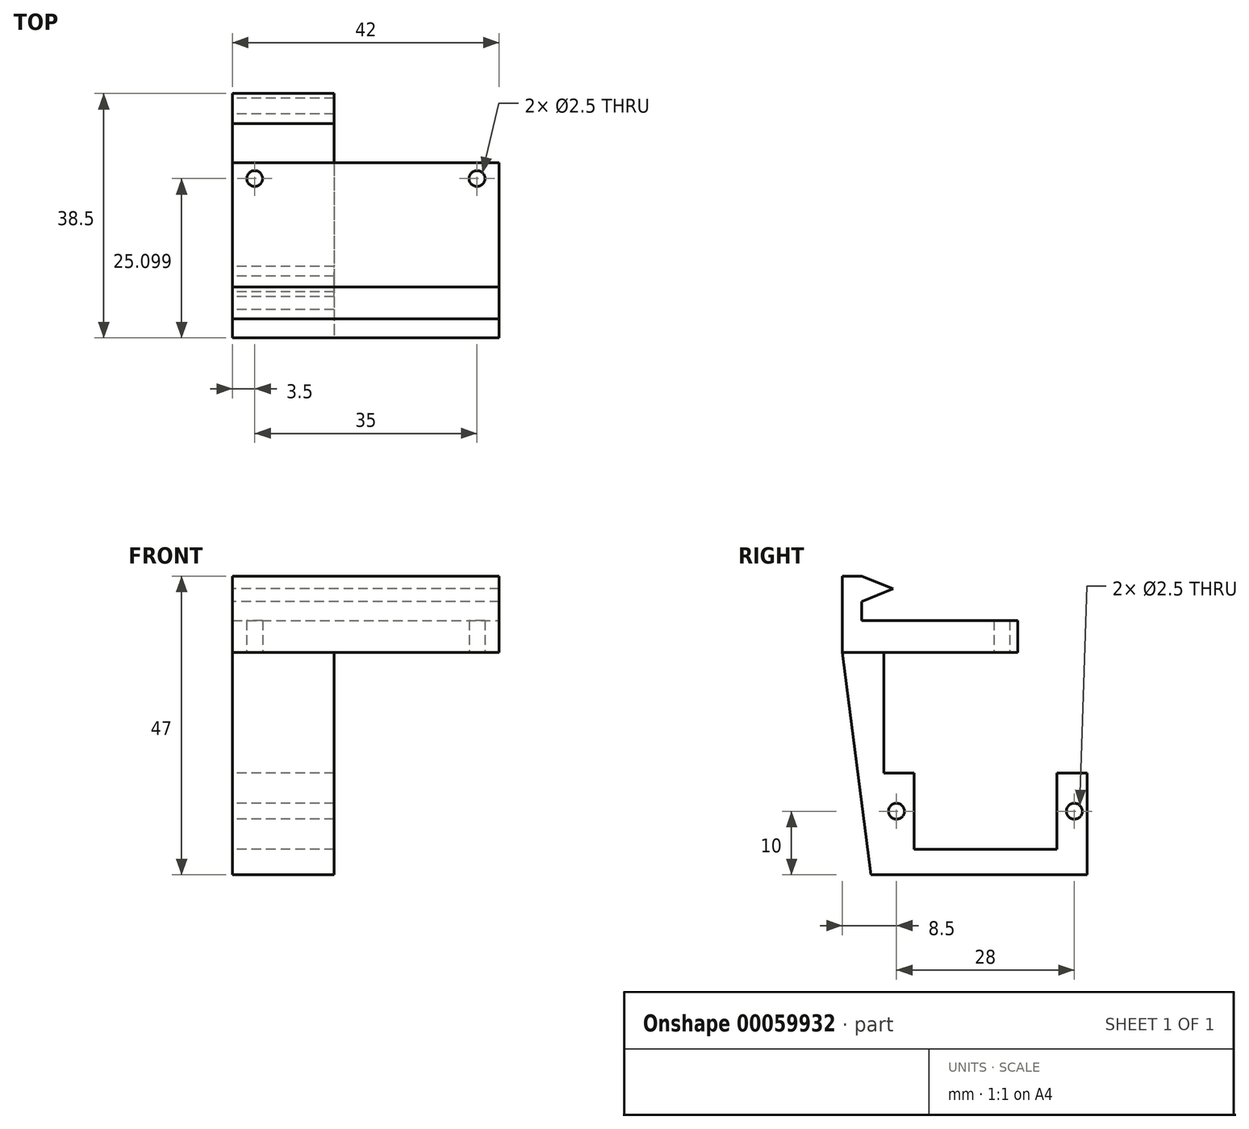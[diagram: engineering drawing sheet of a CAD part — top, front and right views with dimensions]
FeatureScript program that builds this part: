
annotation { "Feature Type Name" : "Feature", "Feature Type Description" : "" }
export const myFeature = defineFeature(function(context is Context, id is Id, definition is map)
    precondition{}
    {
        {
            var Q0;
            Q0=qCreatedBy(makeId("Top.planeOp"),FACE);
            var sketch = newSketch(context, id + "F0", { "sketchPlane" : qUnion([Q0])});
            skLineSegment(sketch, "E0.bottom", {"start": v(0, 0) * mm, "end": v(42, 0) * mm});
            skLineSegment(sketch, "E0.top", {"start": v(0, 24.6) * mm, "end": v(42, 24.6) * mm});
            skLineSegment(sketch, "E0.left", {"start": v(0, 0) * mm, "end": v(0, 24.6) * mm});
            skLineSegment(sketch, "E0.right", {"start": v(42, 0) * mm, "end": v(42, 24.6) * mm});
            skCircle(sketch, "E1", {"center": v(3.5, 22.1) * mm, "radius": 1.25 * mm});
            skCircle(sketch, "E2", {"center": v(38.5, 22.1) * mm, "radius": 1.25 * mm});
            skLineSegment(sketch, "E3", {"start": v(0, 22.1) * mm, "end": v(3.5, 22.1) * mm, "construction": true});
            skLineSegment(sketch, "E4", {"start": v(3.5, 22.1) * mm, "end": v(38.5, 22.1) * mm, "construction": true});
            skLineSegment(sketch, "E5", {"start": v(38.5, 22.1) * mm, "end": v(42, 22.1) * mm, "construction": true});
            skSolve(sketch);
        }
        {
            var Q0;
            Q0=makeQuery(id+"F0.imprint","IMPRINT",FACE,{"disambiguationData":[TD([[makeQuery(id+"F0.imprint","IMPRINT",EDGE,{"derivedFrom":sQuery(id+"F0.wireOp",EDGE,"E0.bottom")}),1.0]])]});
            extrude(context, id + "F1", {"entities" : qUnion([Q0]), "depth" : 5 * mm});
        }
        {
            var Q0;
            Q0=makeQuery(id+"F1.opExtrude","SWEPT_FACE",FACE,{"disambiguationData":[OSD([sQuery(id+"F0.wireOp",EDGE,"E0.left")])]});
            var sketch = newSketch(context, id + "F2", { "sketchPlane" : qUnion([Q0])});
            skLineSegment(sketch, "E6", {"start": v(0, 0) * mm, "end": v(0, 5) * mm});
            skLineSegment(sketch, "E7", {"start": v(0, 8) * mm, "end": v(-5, 10) * mm});
            skLineSegment(sketch, "E8", {"start": v(-5, 10) * mm, "end": v(0, 12) * mm});
            skLineSegment(sketch, "E9", {"start": v(0, 12) * mm, "end": v(3, 12) * mm});
            skLineSegment(sketch, "E10", {"start": v(3, 12) * mm, "end": v(3, 0) * mm});
            skLineSegment(sketch, "E11", {"start": v(3, 0) * mm, "end": v(0, 0) * mm});
            skLineSegment(sketch, "E12", {"start": v(0, 12) * mm, "end": v(0, 8) * mm, "construction": true});
            skLineSegment(sketch, "E13", {"start": v(0, 8) * mm, "end": v(0, 5) * mm});
            skSolve(sketch);
        }
        {
            var Q0;
            Q0=makeQuery(id+"F2.imprint","IMPRINT",FACE,{"disambiguationData":[TD([[makeQuery(id+"F2.imprint","IMPRINT",EDGE,{"derivedFrom":sQuery(id+"F2.wireOp",EDGE,"E6")}),1.0]])]});
            var Q1;
            Q1=makeQuery(id+"F1.opExtrude","SWEPT_FACE",FACE,{"disambiguationData":[OSD([sQuery(id+"F0.wireOp",EDGE,"E0.right")])]});
            extrude(context, id + "F3", {"entities" : qUnion([Q0]), "operationType" : NewBodyOperationType.ADD, "endBound" : BoundingType.UP_TO_SURFACE, "oppositeDirection" : true, "endBoundEntityFace" : qUnion([Q1]), "depth" : 25 * mm});
        }
        {
            var Q0;
            Q0=makeQuery(id+"F3.boolean.opBoolean","MERGE",FACE,{"derivedFrom":[makeQuery(id+"F1.opExtrude","CAP_FACE",FACE,{"disambiguationData":[OSD([sQuery(id+"F0.wireOp",EDGE,"E0.bottom"),sQuery(id+"F0.wireOp",EDGE,"E0.top"),sQuery(id+"F0.wireOp",EDGE,"E0.left"),sQuery(id+"F0.wireOp",EDGE,"E0.right"),sQuery(id+"F0.wireOp",EDGE,"E1"),sQuery(id+"F0.wireOp",EDGE,"E2")])],"isStart":true}),makeQuery(id+"F3.opExtrude","SWEPT_FACE",FACE,{"disambiguationData":[OSD([sQuery(id+"F2.wireOp",EDGE,"E11")])]})]});
            var sketch = newSketch(context, id + "F4", { "sketchPlane" : qUnion([Q0])});
            skLineSegment(sketch, "E14", {"start": v(13.06, 0.88) * mm, "end": v(13.06, -5.19) * mm});
            skLineSegment(sketch, "E15", {"start": v(13.06, -5.19) * mm, "end": v(8.34, -12.26) * mm});
            skLineSegment(sketch, "E16", {"start": v(8.34, -12.26) * mm, "end": v(2.28, -12.26) * mm});
            skLineSegment(sketch, "E17", {"start": v(2.28, -12.26) * mm, "end": v(2.28, 0.88) * mm});
            skLineSegment(sketch, "E18", {"start": v(2.28, 0.88) * mm, "end": v(13.06, 0.88) * mm});
            skLineSegment(sketch, "E19", {"start": v(21, 3) * mm, "end": v(21, -24.6) * mm, "construction": true});
            skArc(sketch, "E20", {"start": v(21, -10.8) * mm, "mid": v(15.68, -16.12) * mm, "end": v(21, -21.43) * mm});
            skArc(sketch, "E21.MirrorCS", {"start": v(21, -10.8) * mm, "mid": v(26.32, -16.12) * mm, "end": v(21, -21.43) * mm});
            skLineSegment(sketch, "E22.MirrorCS", {"start": v(28.94, -5.19) * mm, "end": v(33.66, -12.26) * mm});
            skLineSegment(sketch, "E23.MirrorCS", {"start": v(28.94, 0.88) * mm, "end": v(28.94, -5.19) * mm});
            skLineSegment(sketch, "E24.MirrorCS", {"start": v(39.72, 0.88) * mm, "end": v(28.94, 0.88) * mm});
            skLineSegment(sketch, "E25.MirrorCS", {"start": v(39.72, -12.26) * mm, "end": v(39.72, 0.88) * mm});
            skLineSegment(sketch, "E26.MirrorCS", {"start": v(33.66, -12.26) * mm, "end": v(39.72, -12.26) * mm});
            skSolve(sketch);
        }
        {
            var Q0;
            Q0=qCreatedBy(makeId("Right.planeOp"),FACE);
            var sketch = newSketch(context, id + "F5", { "sketchPlane" : qUnion([Q0])});
            skLineSegment(sketch, "E27", {"start": v(3.5, 0) * mm, "end": v(3.5, -19) * mm});
            skLineSegment(sketch, "E28", {"start": v(3.5, -19) * mm, "end": v(8.25, -19) * mm});
            skLineSegment(sketch, "E29", {"start": v(30.75, -19) * mm, "end": v(35.5, -19) * mm});
            skLineSegment(sketch, "E30", {"start": v(35.5, -19) * mm, "end": v(35.5, -35) * mm});
            skLineSegment(sketch, "E31", {"start": v(35.5, -35) * mm, "end": v(1.46, -35) * mm});
            skLineSegment(sketch, "E32", {"start": v(1.46, -35) * mm, "end": v(-3, 0) * mm});
            skLineSegment(sketch, "E33", {"start": v(3.5, 0) * mm, "end": v(-3, 0) * mm});
            skLineSegment(sketch, "E34", {"start": v(30.75, -19) * mm, "end": v(30.75, -31) * mm});
            skLineSegment(sketch, "E35", {"start": v(8.25, -19) * mm, "end": v(8.25, -31) * mm});
            skLineSegment(sketch, "E36", {"start": v(30.75, -31) * mm, "end": v(8.25, -31) * mm});
            skCircle(sketch, "E37", {"center": v(33.5, -25) * mm, "radius": 1.25 * mm});
            skLineSegment(sketch, "E38", {"start": v(19.5, -31) * mm, "end": v(19.5, -35) * mm, "construction": true});
            skCircle(sketch, "E39.MirrorC", {"center": v(5.5, -25) * mm, "radius": 1.25 * mm});
            skSolve(sketch);
        }
        {
            var Q0;
            Q0 = qSketchRegion(id + "F5", true);
            extrude(context, id + "F6", {"entities" : qUnion([Q0]), "operationType" : NewBodyOperationType.ADD, "depth" : 16 * mm});
        }
    });
